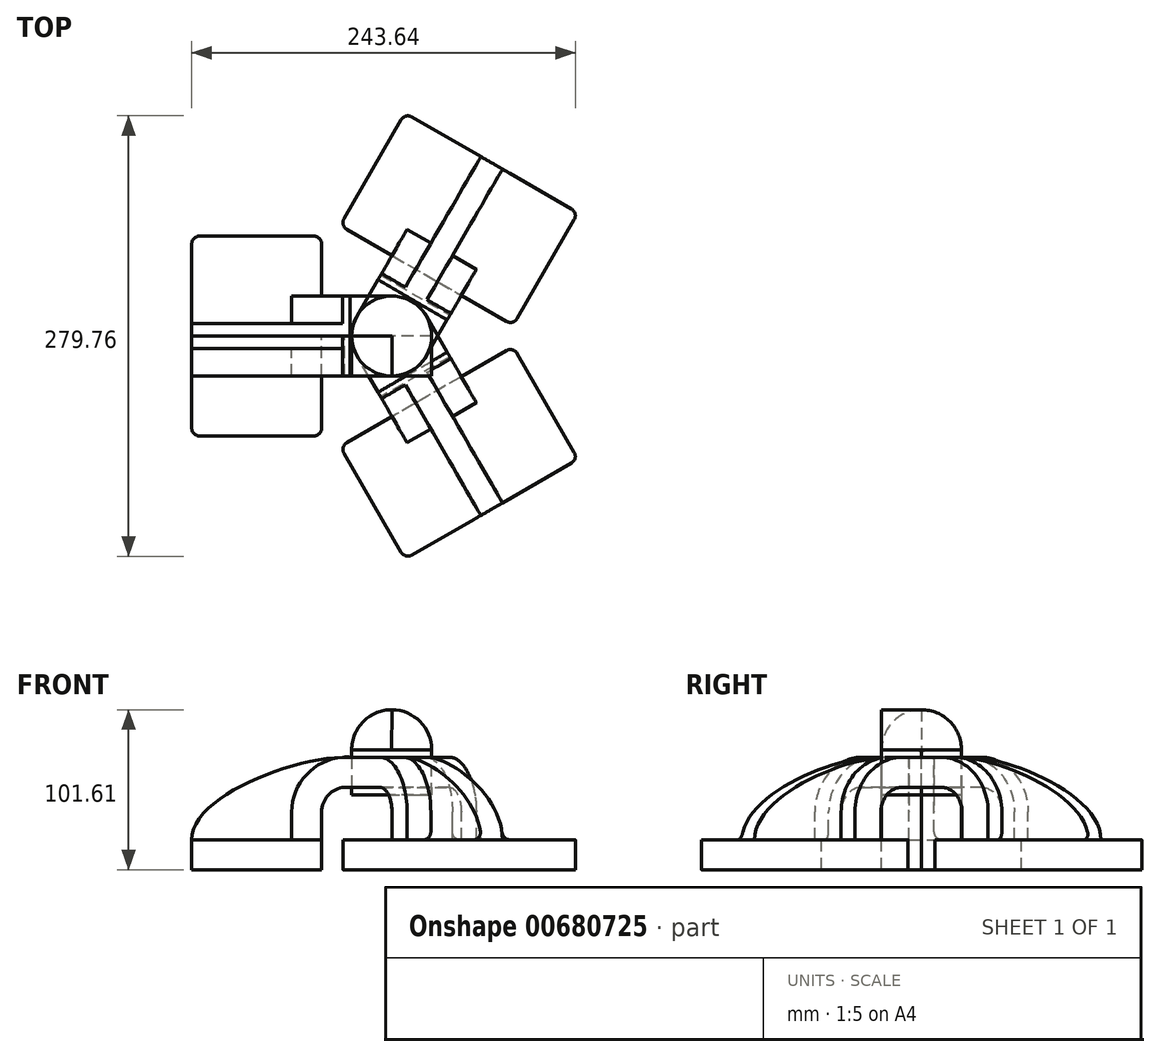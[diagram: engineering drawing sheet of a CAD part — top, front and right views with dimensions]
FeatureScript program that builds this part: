
annotation { "Feature Type Name" : "Feature", "Feature Type Description" : "" }
export const myFeature = defineFeature(function(context is Context, id is Id, definition is map)
    precondition{}
    {
        {
            var Q0;
            Q0=qCreatedBy(makeId("Front.planeOp"),FACE);
            var sketch = newSketch(context, id + "F0", { "sketchPlane" : qUnion([Q0])});
            skLineSegment(sketch, "E0.bottom", {"start": v(41.28, -9.52) * mm, "end": v(-41.28, -9.53) * mm});
            skLineSegment(sketch, "E0.top", {"start": v(41.28, 9.53) * mm, "end": v(-41.28, 9.52) * mm});
            skLineSegment(sketch, "E0.left", {"start": v(41.28, -9.52) * mm, "end": v(41.28, 9.53) * mm});
            skLineSegment(sketch, "E0.right", {"start": v(-41.28, -9.53) * mm, "end": v(-41.28, 9.53) * mm});
            skPoint(sketch, "E0.middle", {"position": v(0, 0) * mm});
            skLineSegment(sketch, "E1.bottom", {"start": v(111.12, 38.1) * mm, "end": v(60.33, 38.1) * mm});
            skLineSegment(sketch, "E1.top", {"start": v(111.12, 66.68) * mm, "end": v(60.32, 66.68) * mm});
            skLineSegment(sketch, "E1.left", {"start": v(111.12, 38.1) * mm, "end": v(111.12, 66.68) * mm});
            skLineSegment(sketch, "E1.right", {"start": v(60.33, 38.1) * mm, "end": v(60.32, 66.68) * mm});
            skPoint(sketch, "E1.middle", {"position": v(85.72, 52.39) * mm});
            skLineSegment(sketch, "E2", {"start": v(41.27, 9.53) * mm, "end": v(41.27, 27.06) * mm});
            skArc(sketch, "E3", {"start": v(55.8, 42.88) * mm, "mid": v(45.46, 37.8) * mm, "end": v(41.27, 27.06) * mm});
            skLineSegment(sketch, "E4", {"start": v(55.8, 42.88) * mm, "end": v(85.72, 42.88) * mm});
            skLineSegment(sketch, "E5.0", {"start": v(59.15, 61.93) * mm, "end": v(85.72, 61.93) * mm});
            skArc(sketch, "E5.1", {"start": v(59.15, 61.93) * mm, "mid": v(33.17, 52.45) * mm, "end": v(22.23, 27.06) * mm});
            skLineSegment(sketch, "E5.2", {"start": v(22.22, 9.53) * mm, "end": v(22.22, 27.06) * mm});
            skLineSegment(sketch, "E6", {"start": v(85.72, 38.1) * mm, "end": v(85.72, 66.68) * mm});
            skFitSpline(sketch, "E7", {"points": [v(-41.28, 9.52) * mm, v(59.15, 61.93) * mm], "startDerivative": vector(-1.58, 81.55) * mm, "endDerivative": vector(107.03, -2.32) * mm});
            skArc(sketch, "E8", {"start": v(86.02, 92.07) * mm, "mid": v(67.87, 84.74) * mm, "end": v(60.32, 66.68) * mm});
            skLineSegment(sketch, "E9", {"start": v(86.02, 92.07) * mm, "end": v(85.72, 66.68) * mm});
            skSolve(sketch);
        }
        {
            var Q0;
            Q0=makeQuery(id+"F0.imprint","IMPRINT",FACE,{"disambiguationData":[TD([[makeQuery(id+"F0.imprint","IMPRINT",EDGE,{"derivedFrom":sQuery(id+"F0.wireOp",EDGE,"E0.bottom")}),-1.0]])]});
            extrude(context, id + "F1", {"entities" : qUnion([Q0]), "endBound" : BoundingType.SYMMETRIC, "depth" : 127 * mm, "offsetDistance" : 25.4 * mm});
        }
        {
            var Q0;
            {var subQ1=sQuery(id+"F0.wireOp",EDGE,"E2");Q0=makeQuery(id+"F0.imprint","IMPRINT",FACE,{"disambiguationData":[TD([[makeQuery(id+"F0.imprint","IMPRINT",EDGE,{"derivedFrom":subQ1}),1.0]])]});}
            var Q1;
            {var subQ0=sQuery(id+"F0.wireOp",EDGE,"E4");var subQ1=sQuery(id+"F0.wireOp",EDGE,"E1.right");var subQ2=makeQuery(id+"F0.imprint","INTERSECT",VERTEX,{"derivedFrom":[subQ1,subQ0]});Q1=makeQuery(id+"F0.imprint","IMPRINT",FACE,{"disambiguationData":[TD([[makeQuery(id+"F0.imprint","IMPRINT",EDGE,{"disambiguationData":[TD([[subQ2,-1.0]])],"derivedFrom":subQ1}),-1.0]])]});}
            extrude(context, id + "F2", {"entities" : qUnion([Q0, Q1]), "operationType" : NewBodyOperationType.ADD, "endBound" : BoundingType.SYMMETRIC, "depth" : 50.8 * mm, "offsetDistance" : 25.4 * mm});
        }
        {
            var Q0;
            {var subQ3=sQuery(id+"F0.wireOp",EDGE,"E5.2");Q0=makeQuery(id+"F0.imprint","IMPRINT",FACE,{"disambiguationData":[TD([[makeQuery(id+"F0.imprint","IMPRINT",EDGE,{"derivedFrom":subQ3}),1.0]])]});}
            extrude(context, id + "F3", {"entities" : qUnion([Q0]), "operationType" : NewBodyOperationType.ADD, "endBound" : BoundingType.SYMMETRIC, "depth" : 15.88 * mm, "offsetDistance" : 25.4 * mm});
        }
        {
            var Q0;
            {var subQ0=sQuery(id+"F0.wireOp",EDGE,"E1.left");Q0=makeQuery(id+"F0.imprint","IMPRINT",FACE,{"disambiguationData":[TD([[makeQuery(id+"F0.imprint","IMPRINT",EDGE,{"derivedFrom":subQ0}),1.0]])]});}
            var Q1;
            Q1=sQuery(id+"F0.wireOp",EDGE,"E6");
            revolve(context, id + "F4", {"operationType" : NewBodyOperationType.ADD, "entities" : qUnion([Q0]), "axis" : qUnion([Q1]), "revolveType" : RevolveType.FULL});
        }
        {
            var Q0;
            Q0=makeQuery(id+"F1.opExtrude","CAP_EDGE",EDGE,{"disambiguationData":[OSD([sQuery(id+"F0.wireOp",EDGE,"E0.left")])],"isStart":false});
            var Q1;
            Q1=makeQuery(id+"F1.opExtrude","CAP_EDGE",EDGE,{"disambiguationData":[OSD([sQuery(id+"F0.wireOp",EDGE,"E0.left")])],"isStart":true});
            var Q2;
            Q2=makeQuery(id+"F1.opExtrude","CAP_EDGE",EDGE,{"disambiguationData":[OSD([sQuery(id+"F0.wireOp",EDGE,"E0.right")])],"isStart":true});
            var Q3;
            Q3=makeQuery(id+"F1.opExtrude","CAP_EDGE",EDGE,{"disambiguationData":[OSD([sQuery(id+"F0.wireOp",EDGE,"E0.right")])],"isStart":false});
            var Q4;
            Q4=makeQuery(id+"F3.opExtrude","CAP_EDGE",EDGE,{"disambiguationData":[OSD([sQuery(id+"F0.wireOp",EDGE,"E0.top")])],"isStart":false});
            var Q5;
            Q5=makeQuery(id+"F3.opExtrude","CAP_EDGE",EDGE,{"disambiguationData":[OSD([sQuery(id+"F0.wireOp",EDGE,"E0.top")])],"isStart":true});
            var Q6;
            Q6=makeQuery(id+"F2.opExtrude","CAP_EDGE",EDGE,{"disambiguationData":[OSD([sQuery(id+"F0.wireOp",EDGE,"E0.top")])],"isStart":false});
            var Q7;
            {var subQ0=sQuery(id+"F0.wireOp",EDGE,"E0.top");var subQ1=sQuery(id+"F0.wireOp",EDGE,"E7");var subQ2=sQuery(id+"F0.wireOp",EDGE,"E5.2");var subQ3=sQuery(id+"F0.wireOp",EDGE,"E5.1");Q7=makeQuery(id+"F3.boolean.opBoolean","SPLIT",EDGE,{"disambiguationData":[TD([makeQuery(id+"F3.opExtrude","CAP_FACE",FACE,{"disambiguationData":[OSD([subQ0,subQ3,subQ2,subQ1])],"isStart":false})])],"derivedFrom":makeQuery(id+"F2.opExtrude","SWEPT_EDGE",EDGE,{"disambiguationData":[OSD([subQ0,subQ2])]})});}
            var Q8;
            {var subQ0=sQuery(id+"F0.wireOp",EDGE,"E0.top");var subQ1=sQuery(id+"F0.wireOp",EDGE,"E7");var subQ2=sQuery(id+"F0.wireOp",EDGE,"E5.2");var subQ3=sQuery(id+"F0.wireOp",EDGE,"E5.1");Q8=makeQuery(id+"F3.boolean.opBoolean","SPLIT",EDGE,{"disambiguationData":[TD([makeQuery(id+"F3.opExtrude","CAP_FACE",FACE,{"disambiguationData":[OSD([subQ0,subQ3,subQ2,subQ1])],"isStart":true})])],"derivedFrom":makeQuery(id+"F2.opExtrude","SWEPT_EDGE",EDGE,{"disambiguationData":[OSD([subQ0,subQ2])]})});}
            var Q9;
            Q9=makeQuery(id+"F2.opExtrude","CAP_EDGE",EDGE,{"disambiguationData":[OSD([sQuery(id+"F0.wireOp",EDGE,"E0.top")])],"isStart":true});
            var Q10;
            Q10=makeQuery(id+"F2.opExtrude","CAP_EDGE",EDGE,{"disambiguationData":[OSD([sQuery(id+"F0.wireOp",EDGE,"E6")])],"isStart":false});
            var Q11;
            Q11=makeQuery(id+"F2.opExtrude","CAP_EDGE",EDGE,{"disambiguationData":[OSD([sQuery(id+"F0.wireOp",EDGE,"E6")])],"isStart":true});
            fillet(context, id + "F5", {"entities" : qUnion([Q0, Q1, Q2, Q3, Q4, Q5, Q6, Q7, Q8, Q9, Q10, Q11]), "radius" : 5.08 * mm, "tangentPropagation" : true, "allowEdgeOverflow" : false});
        }
        {
            var Q0;
            Q0=makeQuery(id+"F1.opExtrude","SWEPT_BODY",BODY,{"disambiguationData":[OSD([sQuery(id+"F0.wireOp",EDGE,"E0.bottom"),sQuery(id+"F0.wireOp",EDGE,"E0.top"),sQuery(id+"F0.wireOp",EDGE,"E0.left"),sQuery(id+"F0.wireOp",EDGE,"E0.right")])]});
            var Q1;
            Q1=sQuery(id+"F0.wireOp",EDGE,"E6");
            circularPattern(context, id + "F6", {"entities" : qUnion([Q0]), "axis" : qUnion([Q1]), "angle" : 360 * degree, "instanceCount" : 3, "equalSpace" : true});
        }
        {
            var Q0;
            {var subQ0=sQuery(id+"F0.wireOp",EDGE,"E8");Q0=makeQuery(id+"F0.imprint","IMPRINT",FACE,{"disambiguationData":[TD([[makeQuery(id+"F0.imprint","IMPRINT",EDGE,{"derivedFrom":subQ0}),1.0]])]});}
            var Q1;
            Q1=sQuery(id+"F0.wireOp",EDGE,"E9");
            revolve(context, id + "F7", {"entities" : qUnion([Q0]), "axis" : qUnion([Q1]), "revolveType" : RevolveType.FULL});
        }
        {
            var Q0;
            Q0 = qSketchRegion(id + "F0", true);
            extrude(context, id + "F8", {"entities" : qUnion([Q0]), "depth" : 25.4 * mm, "offsetDistance" : 25.4 * mm});
        }
    });
